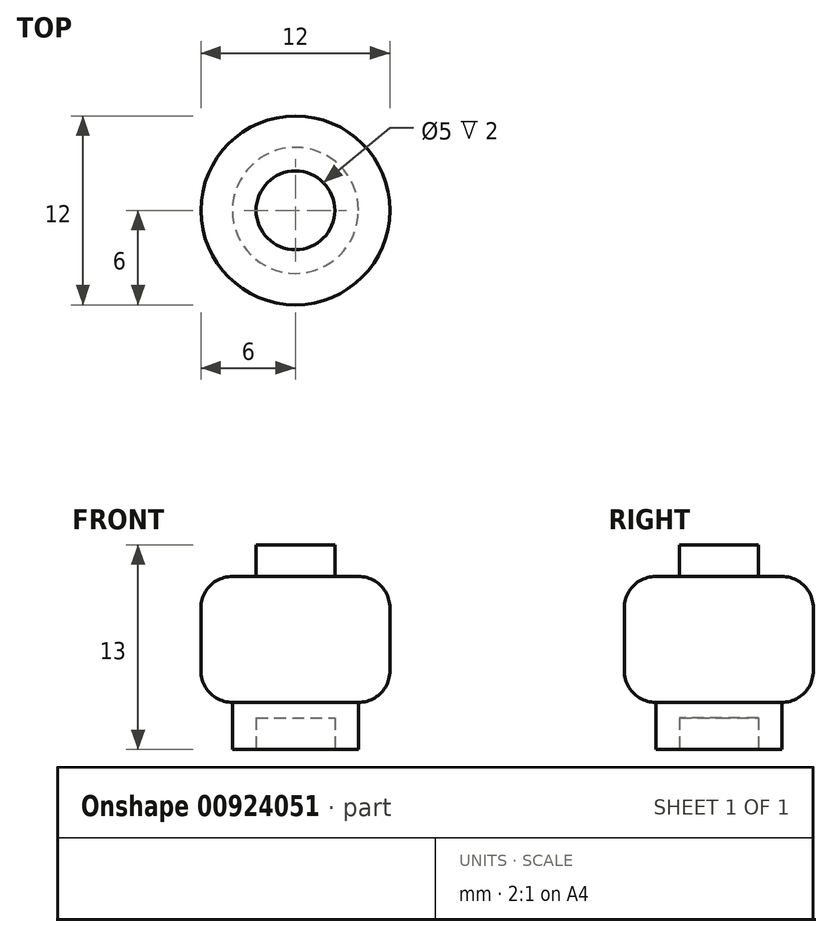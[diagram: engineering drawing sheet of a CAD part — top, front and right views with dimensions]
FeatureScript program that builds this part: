
annotation { "Feature Type Name" : "Feature", "Feature Type Description" : "" }
export const myFeature = defineFeature(function(context is Context, id is Id, definition is map)
    precondition{}
    {
        {
            var Q0;
            Q0=qCreatedBy(makeId("Top.planeOp"),FACE);
            var sketch = newSketch(context, id + "F0", { "sketchPlane" : qUnion([Q0])});
            skCircle(sketch, "E0", {"center": v(0, 0) * mm, "radius": 4 * mm});
            skSolve(sketch);
        }
        {
            var Q0;
            Q0=makeQuery(id+"F0.imprint","IMPRINT",FACE,{"disambiguationData":[TD([[makeQuery(id+"F0.imprint","IMPRINT",EDGE,{"derivedFrom":sQuery(id+"F0.wireOp",EDGE,"E0")}),1.0]])]});
            extrude(context, id + "F1", {"entities" : qUnion([Q0]), "depth" : 3 * mm, "offsetDistance" : 25 * mm});
        }
        {
            var Q0;
            Q0=makeQuery(id+"F1.opExtrude","CAP_FACE",FACE,{"disambiguationData":[OSD([sQuery(id+"F0.wireOp",EDGE,"E0")])],"isStart":false});
            var sketch = newSketch(context, id + "F2", { "sketchPlane" : qUnion([Q0])});
            skCircle(sketch, "E1", {"center": v(0, 0) * mm, "radius": 6 * mm});
            skSolve(sketch);
        }
        {
            var Q0;
            Q0 = qSketchRegion(id + "F2", true);
            extrude(context, id + "F3", {"entities" : qUnion([Q0]), "operationType" : NewBodyOperationType.ADD, "depth" : 8 * mm, "offsetDistance" : 25 * mm});
        }
        {
            var Q0;
            Q0=makeQuery(id+"F3.opExtrude","CAP_FACE",FACE,{"disambiguationData":[OSD([sQuery(id+"F2.wireOp",EDGE,"E1")])],"isStart":false});
            var sketch = newSketch(context, id + "F4", { "sketchPlane" : qUnion([Q0])});
            skCircle(sketch, "E2", {"center": v(0, 0) * mm, "radius": 2.5 * mm});
            skSolve(sketch);
        }
        {
            var Q0;
            Q0=makeQuery(id+"F4.imprint","IMPRINT",FACE,{"disambiguationData":[TD([[makeQuery(id+"F4.imprint","IMPRINT",EDGE,{"derivedFrom":sQuery(id+"F4.wireOp",EDGE,"E2")}),1.0]])]});
            extrude(context, id + "F5", {"entities" : qUnion([Q0]), "operationType" : NewBodyOperationType.ADD, "depth" : 2 * mm, "offsetDistance" : 25 * mm});
        }
        {
            var Q0;
            Q0=makeQuery(id+"F3.opExtrude","CAP_EDGE",EDGE,{"disambiguationData":[OSD([sQuery(id+"F2.wireOp",EDGE,"E1")])],"isStart":false});
            var Q1;
            Q1=makeQuery(id+"F3.opExtrude","CAP_EDGE",EDGE,{"disambiguationData":[OSD([sQuery(id+"F2.wireOp",EDGE,"E1")])],"isStart":true});
            fillet(context, id + "F6", {"entities" : qUnion([Q0, Q1]), "radius" : 2 * mm, "tangentPropagation" : true, "allowEdgeOverflow" : false});
        }
        {
            var Q0;
            Q0=makeQuery(id+"F1.opExtrude","CAP_FACE",FACE,{"disambiguationData":[OSD([sQuery(id+"F0.wireOp",EDGE,"E0")])],"isStart":true});
            var sketch = newSketch(context, id + "F7", { "sketchPlane" : qUnion([Q0])});
            skCircle(sketch, "E3", {"center": v(0, 0) * mm, "radius": 2.5 * mm});
            skSolve(sketch);
        }
        {
            var Q0;
            Q0 = qSketchRegion(id + "F7", true);
            extrude(context, id + "F8", {"entities" : qUnion([Q0]), "operationType" : NewBodyOperationType.REMOVE, "oppositeDirection" : true, "depth" : 2 * mm, "offsetDistance" : 25 * mm});
        }
    });
